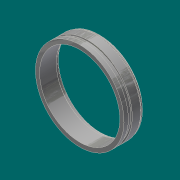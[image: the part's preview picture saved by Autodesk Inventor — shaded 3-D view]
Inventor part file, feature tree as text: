
AUTODESK INVENTOR PART (.ipt)
format: ipt  version: 2017.3 (Build 213256000, 256)  size: 170,496 bytes
history: native  units: in
note: dims shown in document units (in); Inventor stores cm internally (conversion verified against a paired STEP export)
features: revolve x1, chamfer x1, sketch x1
ambient origin geometry x8: Origin, YZ Plane, XZ Plane, XY Plane, X Axis, Y Axis, Z Axis, Center Point
bodies: Solid1 (feature_tree)
feature tree (3):
  revolve  "Revolution1"  [1 undecoded]
  chamfer  "Chamfer2"  Angle=90.0deg  [1 undecoded]
  sketch  "Sketch1"  dims[d0=15.625in d5=6.5in d6=90.0deg d13=16.75in d14=17.25in d16=1.75in d17=1.35in d18=0.0515in d19=0.0842in d20=0.0312in d21=0.125in d22=45.0deg d32=17.0in d33=0.4375in d34=0.1875in d35=0.0625in d36=0.5in d37=0.2577in d38=8.0in d39=0.25in d43=0.5in d44=45.0deg d45=6.5in]
note: 2 required parameter values undecoded (feature->parameter linkage not recoverable at this tier; creation-order binding heuristic only, values carry confidence <= 0.55)